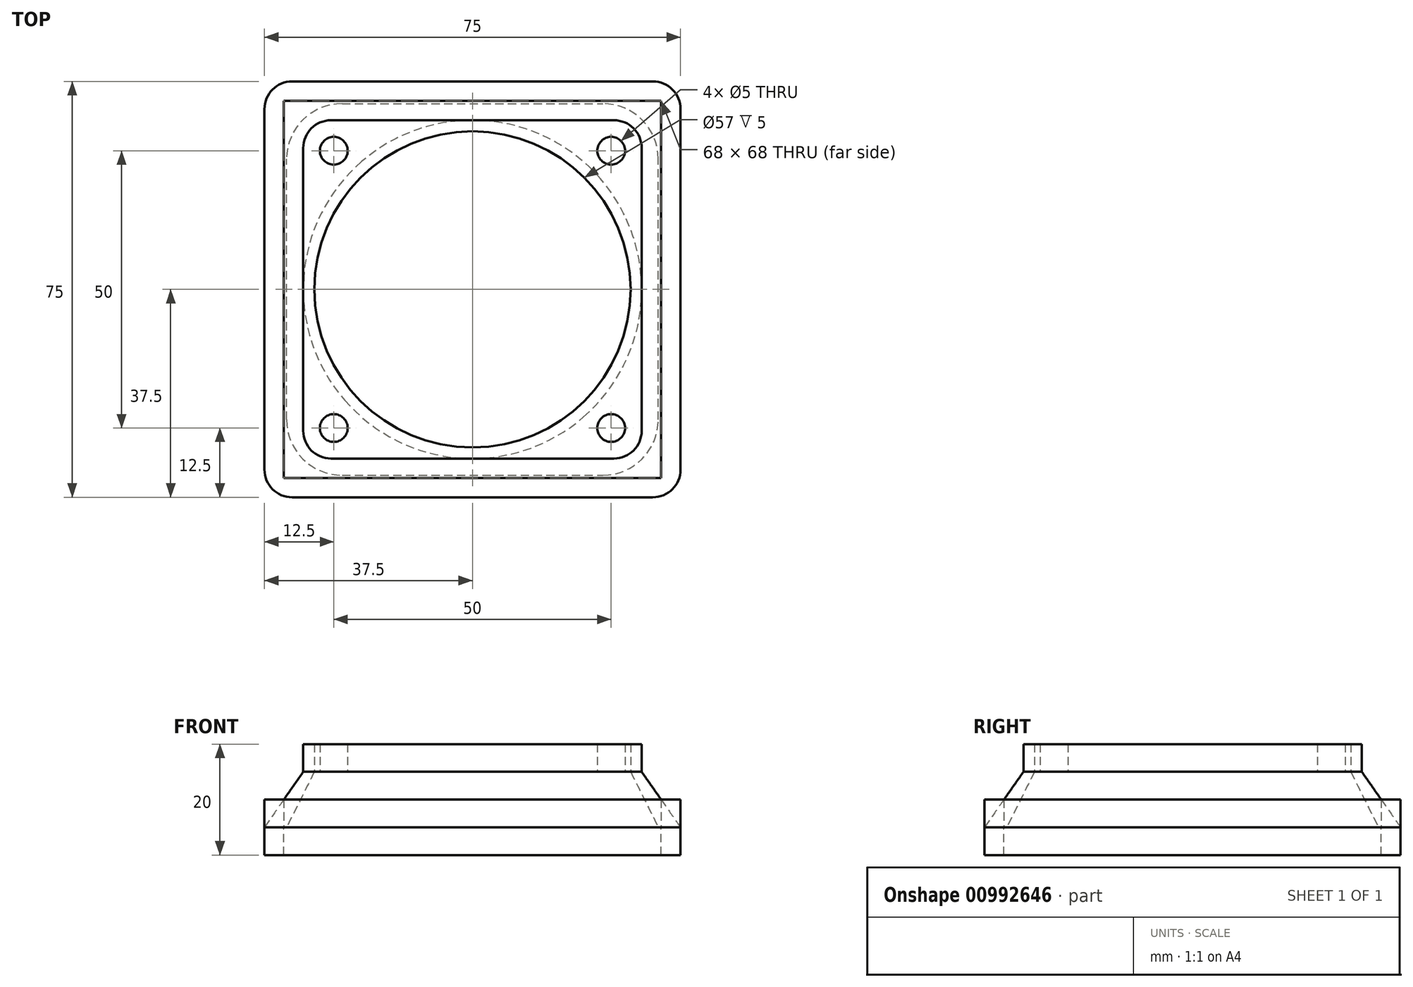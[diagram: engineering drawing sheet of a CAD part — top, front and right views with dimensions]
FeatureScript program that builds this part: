
annotation { "Feature Type Name" : "Feature", "Feature Type Description" : "" }
export const myFeature = defineFeature(function(context is Context, id is Id, definition is map)
    precondition{}
    {
        {
            var Q0;
            Q0=qCreatedBy(makeId("Top.planeOp"),FACE);
            cPlane(context, id + "F0", {"entities" : qUnion([Q0]), "cplaneType" : CPlaneType.OFFSET, "offset" : 10 * mm, "oppositeDirection" : true, "width" : 150 * mm, "height" : 150 * mm});
        }
        {
            var Q0;
            Q0=qCreatedBy(makeId("Top.planeOp"),FACE);
            var sketch = newSketch(context, id + "F1", { "sketchPlane" : qUnion([Q0])});
            skLineSegment(sketch, "E0.bottom", {"start": v(25.5, -30.5) * mm, "end": v(-25.5, -30.5) * mm});
            skLineSegment(sketch, "E0.top", {"start": v(25.5, 30.5) * mm, "end": v(-25.5, 30.5) * mm});
            skLineSegment(sketch, "E0.left", {"start": v(30.5, -25.5) * mm, "end": v(30.5, 25.5) * mm});
            skLineSegment(sketch, "E0.right", {"start": v(-30.5, -25.5) * mm, "end": v(-30.5, 25.5) * mm});
            skPoint(sketch, "E0.middle", {"position": v(0, 0) * mm});
            skPoint(sketch, "E1.visualSharp", {"position": v(30.5, -30.5) * mm});
            skArc(sketch, "E1.filletArc", {"start": v(25.5, -30.5) * mm, "mid": v(29.04, -29.04) * mm, "end": v(30.5, -25.5) * mm});
            skPoint(sketch, "E2.visualSharp", {"position": v(30.5, 30.5) * mm});
            skArc(sketch, "E2.filletArc", {"start": v(30.5, 25.5) * mm, "mid": v(29.04, 29.04) * mm, "end": v(25.5, 30.5) * mm});
            skPoint(sketch, "E3.visualSharp", {"position": v(-30.5, 30.5) * mm});
            skArc(sketch, "E3.filletArc", {"start": v(-25.5, 30.5) * mm, "mid": v(-29.04, 29.04) * mm, "end": v(-30.5, 25.5) * mm});
            skPoint(sketch, "E4.visualSharp", {"position": v(-30.5, -30.5) * mm});
            skArc(sketch, "E4.filletArc", {"start": v(-30.5, -25.5) * mm, "mid": v(-29.04, -29.04) * mm, "end": v(-25.5, -30.5) * mm});
            skSolve(sketch);
        }
        {
            var Q0;
            Q0=qCreatedBy(id+"F0.planeOp",FACE);
            var sketch = newSketch(context, id + "F2", { "sketchPlane" : qUnion([Q0])});
            skLineSegment(sketch, "E5.bottom", {"start": v(-23.5, -33.5) * mm, "end": v(23.5, -33.5) * mm});
            skLineSegment(sketch, "E5.top", {"start": v(-23.5, 33.5) * mm, "end": v(23.5, 33.5) * mm});
            skLineSegment(sketch, "E5.left", {"start": v(-33.5, -23.5) * mm, "end": v(-33.5, 23.5) * mm});
            skLineSegment(sketch, "E5.right", {"start": v(33.5, -23.5) * mm, "end": v(33.5, 23.5) * mm});
            skPoint(sketch, "E5.middle", {"position": v(0, 0) * mm});
            skPoint(sketch, "E6.visualSharp", {"position": v(-33.5, 33.5) * mm});
            skArc(sketch, "E6.filletArc", {"start": v(-23.5, 33.5) * mm, "mid": v(-30.57, 30.57) * mm, "end": v(-33.5, 23.5) * mm});
            skPoint(sketch, "E7.visualSharp", {"position": v(33.5, 33.5) * mm});
            skArc(sketch, "E7.filletArc", {"start": v(33.5, 23.5) * mm, "mid": v(30.57, 30.57) * mm, "end": v(23.5, 33.5) * mm});
            skPoint(sketch, "E8.visualSharp", {"position": v(33.5, -33.5) * mm});
            skArc(sketch, "E8.filletArc", {"start": v(23.5, -33.5) * mm, "mid": v(30.57, -30.57) * mm, "end": v(33.5, -23.5) * mm});
            skPoint(sketch, "E9.visualSharp", {"position": v(-33.5, -33.5) * mm});
            skArc(sketch, "E9.filletArc", {"start": v(-33.5, -23.5) * mm, "mid": v(-30.57, -30.57) * mm, "end": v(-23.5, -33.5) * mm});
            skSolve(sketch);
        }
        {
            var Q0;
            Q0=qCreatedBy(makeId("Top.planeOp"),FACE);
            var sketch = newSketch(context, id + "F3", { "sketchPlane" : qUnion([Q0])});
            skCircle(sketch, "E10", {"center": v(0, 0) * mm, "radius": 28.5 * mm});
            skSolve(sketch);
        }
        {
            var Q0;
            Q0=qCreatedBy(id+"F0.planeOp",FACE);
            var sketch = newSketch(context, id + "F4", { "sketchPlane" : qUnion([Q0])});
            skLineSegment(sketch, "E11.bottom", {"start": v(32.5, -37.5) * mm, "end": v(-32.5, -37.5) * mm});
            skLineSegment(sketch, "E11.top", {"start": v(32.5, 37.5) * mm, "end": v(-32.5, 37.5) * mm});
            skLineSegment(sketch, "E11.left", {"start": v(37.5, -32.5) * mm, "end": v(37.5, 32.5) * mm});
            skLineSegment(sketch, "E11.right", {"start": v(-37.5, -32.5) * mm, "end": v(-37.5, 32.5) * mm});
            skPoint(sketch, "E11.middle", {"position": v(0, 0) * mm});
            skPoint(sketch, "E12.visualSharp", {"position": v(37.5, -37.5) * mm});
            skArc(sketch, "E12.filletArc", {"start": v(32.5, -37.5) * mm, "mid": v(36.04, -36.04) * mm, "end": v(37.5, -32.5) * mm});
            skPoint(sketch, "E13.visualSharp", {"position": v(37.5, 37.5) * mm});
            skArc(sketch, "E13.filletArc", {"start": v(37.5, 32.5) * mm, "mid": v(36.04, 36.04) * mm, "end": v(32.5, 37.5) * mm});
            skPoint(sketch, "E14.visualSharp", {"position": v(-37.5, 37.5) * mm});
            skArc(sketch, "E14.filletArc", {"start": v(-32.5, 37.5) * mm, "mid": v(-36.04, 36.04) * mm, "end": v(-37.5, 32.5) * mm});
            skPoint(sketch, "E15.visualSharp", {"position": v(-37.5, -37.5) * mm});
            skArc(sketch, "E15.filletArc", {"start": v(-37.5, -32.5) * mm, "mid": v(-36.04, -36.04) * mm, "end": v(-32.5, -37.5) * mm});
            skSolve(sketch);
        }
        {
            var Q0;
            Q0=qCreatedBy(makeId("Top.planeOp"),FACE);
            var sketch = newSketch(context, id + "F5", { "sketchPlane" : qUnion([Q0])});
            skCircle(sketch, "E16", {"center": v(0, 0) * mm, "radius": 30.5 * mm});
            skSolve(sketch);
        }
        {
            var Q0;
            Q0=qCreatedBy(id+"F0.planeOp",FACE);
            var sketch = newSketch(context, id + "F6", { "sketchPlane" : qUnion([Q0])});
            skLineSegment(sketch, "E17.bottom", {"start": v(-34, -34) * mm, "end": v(34, -34) * mm});
            skLineSegment(sketch, "E17.top", {"start": v(-34, 34) * mm, "end": v(34, 34) * mm});
            skLineSegment(sketch, "E17.left", {"start": v(-34, -34) * mm, "end": v(-34, 34) * mm});
            skLineSegment(sketch, "E17.right", {"start": v(34, -34) * mm, "end": v(34, 34) * mm});
            skPoint(sketch, "E17.middle", {"position": v(0, 0) * mm});
            skSolve(sketch);
        }
        {
            var Q0;
            Q0=qSketchRegion(id+"F9",true);
            var Q1;
            Q1=qSketchRegion(id+"F1",true);
            extrude(context, id + "F7", {"entities" : qUnion([Q0, Q1]), "depth" : 5 * mm, "offsetDistance" : 25 * mm});
        }
        {
            var Q0;
            Q0=qCreatedBy(makeId("Top.planeOp"),FACE);
            var sketch = newSketch(context, id + "F8", { "sketchPlane" : qUnion([Q0])});
            skLineSegment(sketch, "E18.bottom", {"start": v(-25, 25) * mm, "end": v(25, 25) * mm, "construction": true});
            skLineSegment(sketch, "E18.top", {"start": v(-25, -25) * mm, "end": v(25, -25) * mm, "construction": true});
            skLineSegment(sketch, "E18.left", {"start": v(-25, 25) * mm, "end": v(-25, -25) * mm, "construction": true});
            skLineSegment(sketch, "E18.right", {"start": v(25, 25) * mm, "end": v(25, -25) * mm, "construction": true});
            skPoint(sketch, "E18.middle", {"position": v(0, 0) * mm});
            skSolve(sketch);
        }
        {
            var Q0;
            Q0=qCreatedBy(makeId("Top.planeOp"),FACE);
            var sketch = newSketch(context, id + "F9", { "sketchPlane" : qUnion([Q0])});
            skCircle(sketch, "E19", {"center": v(-25, 25) * mm, "radius": 2.5 * mm});
            skCircle(sketch, "E20", {"center": v(25, 25) * mm, "radius": 2.5 * mm});
            skCircle(sketch, "E21", {"center": v(25, -25) * mm, "radius": 2.5 * mm});
            skCircle(sketch, "E22", {"center": v(-25, -25) * mm, "radius": 2.5 * mm});
            skSolve(sketch);
        }
        {
            var Q0;
            Q0=qSketchRegion(id+"F3",true);
            var Q1;
            Q1=qSketchRegion(id+"F6",true);
            var Q2;
            Q2=qSketchRegion(id+"F4",true);
            extrude(context, id + "F10", {"entities" : qUnion([Q0, Q1, Q2]), "depth" : 5 * mm, "offsetDistance" : 25 * mm});
        }
        {
            var Q0;
            Q0=qSketchRegion(id+"F9",true);
            extrude(context, id + "F11", {"entities" : qUnion([Q0]), "depth" : 5 * mm, "offsetDistance" : 25 * mm});
        }
        {
            var Q0;
            Q0=makeQuery(id+"F10.opExtrude","SWEPT_BODY",BODY,{"disambiguationData":[OSD([sQuery(id+"F3.wireOp",EDGE,"E10")])]});
            var Q1;
            Q1=makeQuery(id+"F11.opExtrude","SWEPT_BODY",BODY,{"disambiguationData":[OSD([sQuery(id+"F9.wireOp",EDGE,"E20")])]});
            var Q2;
            Q2=makeQuery(id+"F11.opExtrude","SWEPT_BODY",BODY,{"disambiguationData":[OSD([sQuery(id+"F9.wireOp",EDGE,"E22")])]});
            var Q3;
            Q3=makeQuery(id+"F11.opExtrude","SWEPT_BODY",BODY,{"disambiguationData":[OSD([sQuery(id+"F9.wireOp",EDGE,"E19")])]});
            var Q4;
            Q4=makeQuery(id+"F11.opExtrude","SWEPT_BODY",BODY,{"disambiguationData":[OSD([sQuery(id+"F9.wireOp",EDGE,"E21")])]});
            var Q5;
            Q5=makeQuery(id+"F7.opExtrude","SWEPT_BODY",BODY,{"disambiguationData":[OSD([sQuery(id+"F1.wireOp",EDGE,"E0.bottom"),sQuery(id+"F1.wireOp",EDGE,"E0.top"),sQuery(id+"F1.wireOp",EDGE,"E0.left"),sQuery(id+"F1.wireOp",EDGE,"E0.right"),sQuery(id+"F1.wireOp",EDGE,"E1.filletArc"),sQuery(id+"F1.wireOp",EDGE,"E2.filletArc"),sQuery(id+"F1.wireOp",EDGE,"E3.filletArc"),sQuery(id+"F1.wireOp",EDGE,"E4.filletArc")])]});
            booleanBodies(context, id + "F12", {"operationType" : BooleanOperationType.SUBTRACTION, "tools" : qUnion([Q0, Q1, Q2, Q3, Q4]), "targets" : qUnion([Q5])});
        }
        {
            var Q0;
            Q0=qSketchRegion(id+"F3",true);
            var Q1;
            Q1=qSketchRegion(id+"F2",true);
            loft(context, id + "F13", {"sheetProfilesArray" : [{ "sheetProfileEntities" : qUnion([Q0]) }, { "sheetProfileEntities" : qUnion([Q1]) }]});
        }
        {
            var Q0;
            Q0=qSketchRegion(id+"F5",true);
            var Q1;
            Q1=qSketchRegion(id+"F4",true);
            loft(context, id + "F14", {"sheetProfilesArray" : [{ "sheetProfileEntities" : qUnion([Q0]) }, { "sheetProfileEntities" : qUnion([Q1]) }]});
        }
        {
            var Q0;
            Q0=makeQuery(id+"F13.opLoft","SWEPT_BODY",BODY,{"disambiguationData":[OSD([makeQuery(id+"F2.imprint","IMPRINT",FACE,{"disambiguationData":[TD([[makeQuery(id+"F2.imprint","IMPRINT",EDGE,{"derivedFrom":sQuery(id+"F2.wireOp",EDGE,"E5.bottom")}),1.0]])]}),makeQuery(id+"F3.imprint","IMPRINT",FACE,{"disambiguationData":[TD([[makeQuery(id+"F3.imprint","IMPRINT",EDGE,{"derivedFrom":sQuery(id+"F3.wireOp",EDGE,"E10")}),1.0]])]})])]});
            var Q1;
            Q1=makeQuery(id+"F14.opLoft","SWEPT_BODY",BODY,{"disambiguationData":[OSD([makeQuery(id+"F4.imprint","IMPRINT",FACE,{"disambiguationData":[TD([[makeQuery(id+"F4.imprint","IMPRINT",EDGE,{"derivedFrom":sQuery(id+"F4.wireOp",EDGE,"E11.bottom")}),-1.0]])]}),makeQuery(id+"F5.imprint","IMPRINT",FACE,{"disambiguationData":[TD([[makeQuery(id+"F5.imprint","IMPRINT",EDGE,{"derivedFrom":sQuery(id+"F5.wireOp",EDGE,"E16")}),1.0]])]})])]});
            booleanBodies(context, id + "F15", {"operationType" : BooleanOperationType.SUBTRACTION, "tools" : qUnion([Q0]), "targets" : qUnion([Q1])});
        }
        {
            var Q0;
            Q0=makeQuery(id+"F4.imprint","IMPRINT",FACE,{"disambiguationData":[TD([[makeQuery(id+"F4.imprint","IMPRINT",EDGE,{"derivedFrom":sQuery(id+"F4.wireOp",EDGE,"E11.bottom")}),-1.0]])]});
            extrude(context, id + "F16", {"entities" : qUnion([Q0]), "flatOperationType" : FlatOperationType.REMOVE, "oppositeDirection" : true, "depth" : 5 * mm, "offsetDistance" : 25 * mm, "domain" : OperationDomain.MODEL});
        }
        {
            var Q0;
            Q0=qSketchRegion(id+"F6",true);
            extrude(context, id + "F17", {"entities" : qUnion([Q0]), "flatOperationType" : FlatOperationType.REMOVE, "oppositeDirection" : true, "depth" : 10 * mm, "offsetDistance" : 25 * mm, "domain" : OperationDomain.MODEL});
        }
        {
            var Q0;
            Q0=makeQuery(id+"F17.opExtrude","SWEPT_BODY",BODY,{"disambiguationData":[OSD([sQuery(id+"F6.wireOp",EDGE,"E17.bottom"),sQuery(id+"F6.wireOp",EDGE,"E17.top"),sQuery(id+"F6.wireOp",EDGE,"E17.left"),sQuery(id+"F6.wireOp",EDGE,"E17.right")])]});
            var Q1;
            Q1=makeQuery(id+"F16.opExtrude","SWEPT_BODY",BODY,{"disambiguationData":[OSD([sQuery(id+"F4.wireOp",EDGE,"E11.bottom"),sQuery(id+"F4.wireOp",EDGE,"E11.top"),sQuery(id+"F4.wireOp",EDGE,"E11.left"),sQuery(id+"F4.wireOp",EDGE,"E11.right"),sQuery(id+"F4.wireOp",EDGE,"E12.filletArc"),sQuery(id+"F4.wireOp",EDGE,"E13.filletArc"),sQuery(id+"F4.wireOp",EDGE,"E14.filletArc"),sQuery(id+"F4.wireOp",EDGE,"E15.filletArc")])]});
            booleanBodies(context, id + "F18", {"operationType" : BooleanOperationType.SUBTRACTION, "tools" : qUnion([Q0]), "targets" : qUnion([Q1])});
        }
    });
